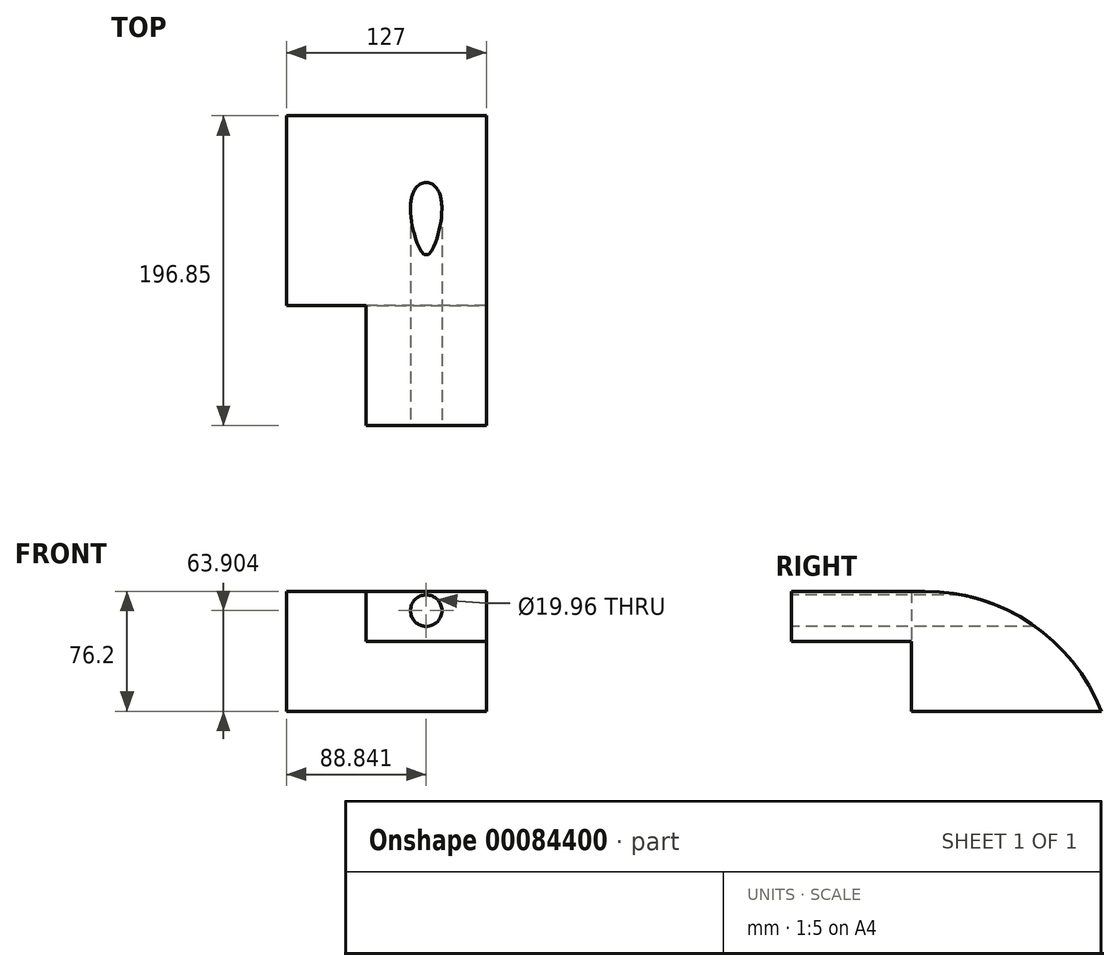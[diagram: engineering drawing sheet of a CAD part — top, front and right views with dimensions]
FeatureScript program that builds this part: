
annotation { "Feature Type Name" : "Feature", "Feature Type Description" : "" }
export const myFeature = defineFeature(function(context is Context, id is Id, definition is map)
    precondition{}
    {
        {
            var Q0;
            Q0=qCreatedBy(makeId("Top.planeOp"),FACE);
            var sketch = newSketch(context, id + "F0", { "sketchPlane" : qUnion([Q0])});
            skLineSegment(sketch, "E0.bottom", {"start": v(-38.06, -65.18) * mm, "end": v(88.94, -65.18) * mm});
            skLineSegment(sketch, "E0.top", {"start": v(-38.06, 55.47) * mm, "end": v(88.94, 55.47) * mm});
            skLineSegment(sketch, "E0.left", {"start": v(-38.06, -65.18) * mm, "end": v(-38.06, 55.47) * mm});
            skLineSegment(sketch, "E0.right", {"start": v(88.94, -65.18) * mm, "end": v(88.94, 55.47) * mm});
            skSolve(sketch);
        }
        {
            var Q0;
            Q0=makeQuery(id+"F0.imprint","IMPRINT",FACE,{"disambiguationData":[TD([[makeQuery(id+"F0.imprint","IMPRINT",EDGE,{"derivedFrom":sQuery(id+"F0.wireOp",EDGE,"E0.bottom")}),1.0]])]});
            extrude(context, id + "F1", {"entities" : qUnion([Q0]), "depth" : 76.2 * mm});
        }
        {
            var Q0;
            Q0=makeQuery(id+"F1.opExtrude","CAP_EDGE",EDGE,{"disambiguationData":[OSD([sQuery(id+"F0.wireOp",EDGE,"E0.top")])],"isStart":false});
            fillet(context, id + "F2", {"entities" : qUnion([Q0]), "radius" : 120.65 * mm, "tangentPropagation" : true, "allowEdgeOverflow" : false});
        }
        {
            var Q0;
            Q0=makeQuery(id+"F1.opExtrude","SWEPT_FACE",FACE,{"disambiguationData":[OSD([sQuery(id+"F0.wireOp",EDGE,"E0.bottom")])]});
            var sketch = newSketch(context, id + "F3", { "sketchPlane" : qUnion([Q0])});
            skLineSegment(sketch, "E1.bottom", {"start": v(88.94, 76.2) * mm, "end": v(12.74, 76.2) * mm});
            skLineSegment(sketch, "E1.top", {"start": v(88.94, 44.45) * mm, "end": v(12.74, 44.45) * mm});
            skLineSegment(sketch, "E1.left", {"start": v(88.94, 76.2) * mm, "end": v(88.94, 44.45) * mm});
            skLineSegment(sketch, "E1.right", {"start": v(12.74, 76.2) * mm, "end": v(12.74, 44.45) * mm});
            skSolve(sketch);
        }
        {
            var Q0;
            Q0=makeQuery(id+"F3.imprint","IMPRINT",FACE,{"disambiguationData":[TD([[makeQuery(id+"F3.imprint","IMPRINT",EDGE,{"derivedFrom":sQuery(id+"F3.wireOp",EDGE,"E1.bottom")}),-1.0]])]});
            extrude(context, id + "F4", {"entities" : qUnion([Q0]), "operationType" : NewBodyOperationType.ADD, "depth" : 76.2 * mm});
        }
        {
            var Q0;
            Q0=makeQuery(id+"F4.opExtrude","CAP_FACE",FACE,{"disambiguationData":[OSD([sQuery(id+"F3.wireOp",EDGE,"E1.bottom"),sQuery(id+"F3.wireOp",EDGE,"E1.top"),sQuery(id+"F3.wireOp",EDGE,"E1.left"),sQuery(id+"F3.wireOp",EDGE,"E1.right")])],"isStart":false});
            var sketch = newSketch(context, id + "F5", { "sketchPlane" : qUnion([Q0])});
            skCircle(sketch, "E2", {"center": v(50.78, 63.9) * mm, "radius": 9.98 * mm});
            skSolve(sketch);
        }
        {
            var Q0;
            Q0=makeQuery(id+"F5.imprint","IMPRINT",FACE,{"disambiguationData":[TD([[makeQuery(id+"F5.imprint","IMPRINT",EDGE,{"derivedFrom":sQuery(id+"F5.wireOp",EDGE,"E2")}),1.0]])]});
            var Q1;
            Q1=sQuery(id+"F5.wireOp",EDGE,"E2");
            extrude(context, id + "F6", {"entities" : qUnion([Q0]), "operationType" : NewBodyOperationType.REMOVE, "surfaceEntities" : qUnion([Q1]), "oppositeDirection" : true, "depth" : 215.9 * mm});
        }
    });
